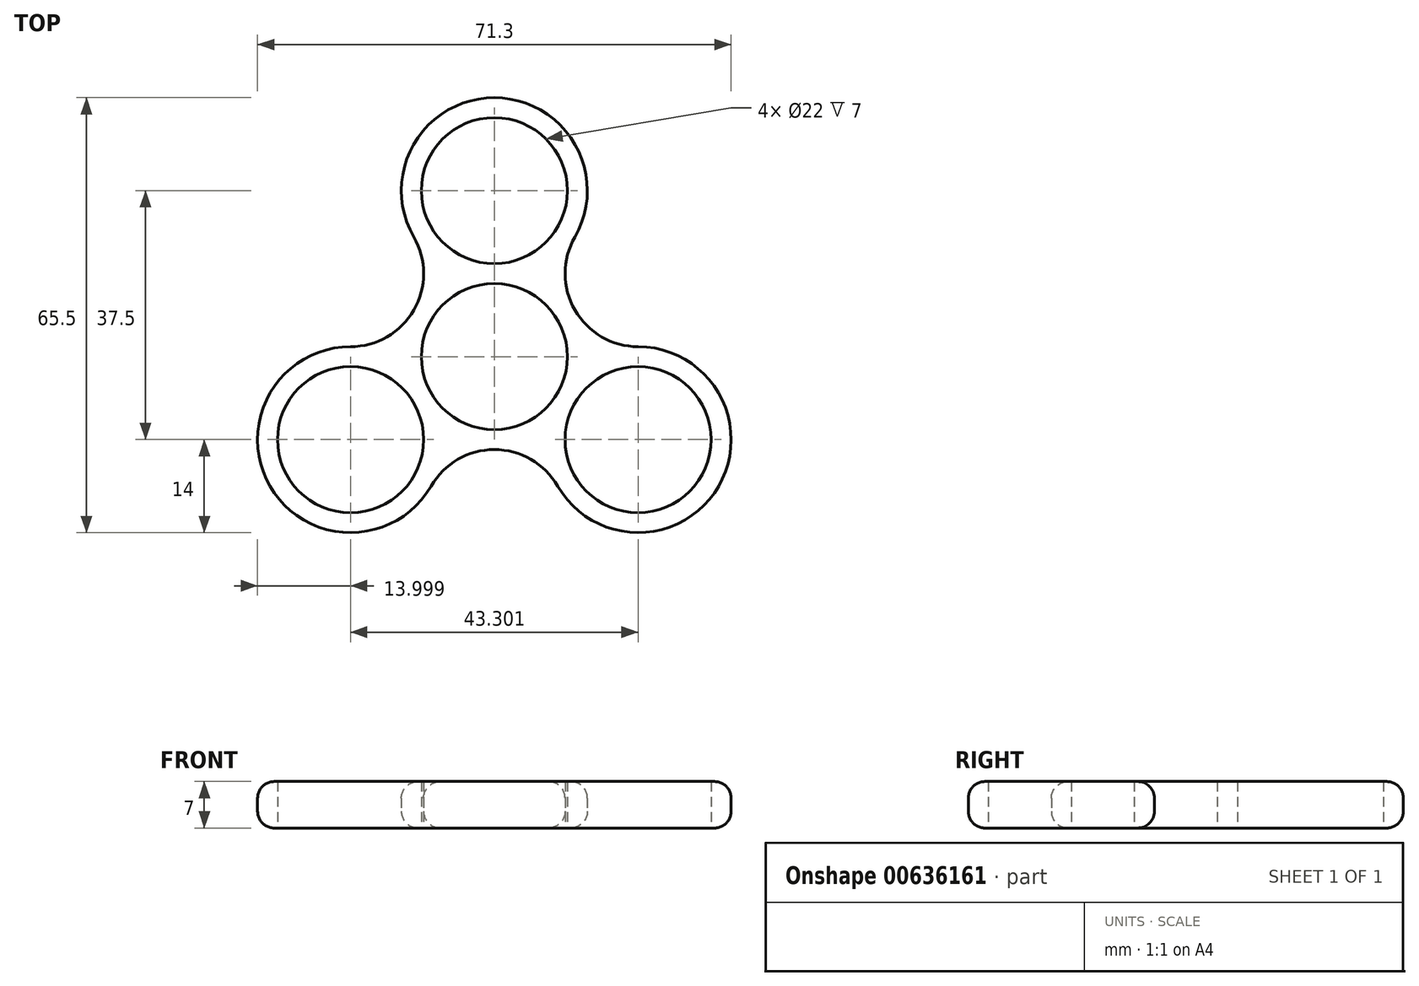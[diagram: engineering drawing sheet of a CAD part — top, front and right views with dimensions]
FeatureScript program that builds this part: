
annotation { "Feature Type Name" : "Feature", "Feature Type Description" : "" }
export const myFeature = defineFeature(function(context is Context, id is Id, definition is map)
    precondition{}
    {
        {
            var Q0;
            Q0=qCreatedBy(makeId("Top.planeOp"),FACE);
            var sketch = newSketch(context, id + "F0", { "sketchPlane" : qUnion([Q0])});
            skCircle(sketch, "E0", {"center": v(0, 0) * mm, "radius": 11 * mm});
            skCircle(sketch, "E1", {"center": v(0, 0) * mm, "radius": 25 * mm});
            skCircle(sketch, "E2", {"center": v(0, 0) * mm, "radius": 39 * mm});
            skCircle(sketch, "E3", {"center": v(0, 25) * mm, "radius": 11 * mm});
            skCircle(sketch, "E4.1.0", {"center": v(-21.65, 12.5) * mm, "radius": 11 * mm});
            skCircle(sketch, "E4.2.0", {"center": v(-21.65, -12.5) * mm, "radius": 11 * mm});
            skCircle(sketch, "E4.3.0", {"center": v(0, -25) * mm, "radius": 11 * mm});
            skCircle(sketch, "E4.4.0", {"center": v(21.65, -12.5) * mm, "radius": 11 * mm});
            skCircle(sketch, "E4.5.0", {"center": v(21.65, 12.5) * mm, "radius": 11 * mm});
            skCircle(sketch, "E5", {"center": v(0, 25) * mm, "radius": 14 * mm});
            skCircle(sketch, "E6.1.0", {"center": v(-21.65, -12.5) * mm, "radius": 14 * mm});
            skCircle(sketch, "E6.2.0", {"center": v(21.65, -12.5) * mm, "radius": 14 * mm});
            skSolve(sketch);
        }
        {
            var Q0;
            {var subQ0=sQuery(id+"F0.wireOp",EDGE,"E5");var subQ2=sQuery(id+"F0.wireOp",EDGE,"E1");var subQ7=makeQuery(id+"F0.imprint","INTERSECT",VERTEX,{"disambiguationData":[OD(0.0)],"derivedFrom":[subQ2,subQ0]});Q0=makeQuery(id+"F0.imprint","IMPRINT",FACE,{"disambiguationData":[TD([[makeQuery(id+"F0.imprint","IMPRINT",EDGE,{"disambiguationData":[TD([[subQ7,-1.0]])],"derivedFrom":subQ2}),-1.0]])]});}
            var Q1;
            {var subQ0=sQuery(id+"F0.wireOp",EDGE,"E6.1.0");var subQ2=sQuery(id+"F0.wireOp",EDGE,"E1");var subQ7=makeQuery(id+"F0.imprint","INTERSECT",VERTEX,{"disambiguationData":[OD(0.0)],"derivedFrom":[subQ2,subQ0]});Q1=makeQuery(id+"F0.imprint","IMPRINT",FACE,{"disambiguationData":[TD([[makeQuery(id+"F0.imprint","IMPRINT",EDGE,{"disambiguationData":[TD([[subQ7,-1.0]])],"derivedFrom":subQ2}),-1.0]])]});}
            var Q2;
            {var subQ0=sQuery(id+"F0.wireOp",EDGE,"E6.2.0");var subQ2=sQuery(id+"F0.wireOp",EDGE,"E1");var subQ7=makeQuery(id+"F0.imprint","INTERSECT",VERTEX,{"disambiguationData":[OD(1.0)],"derivedFrom":[subQ2,subQ0]});Q2=makeQuery(id+"F0.imprint","IMPRINT",FACE,{"disambiguationData":[TD([[makeQuery(id+"F0.imprint","IMPRINT",EDGE,{"disambiguationData":[TD([[subQ7,-1.0]])],"derivedFrom":subQ2}),-1.0]])]});}
            var Q3;
            {var subQ1=sQuery(id+"F0.wireOp",EDGE,"E1");var subQ4=sQuery(id+"F0.wireOp",EDGE,"E6.1.0");var subQ5=makeQuery(id+"F0.imprint","INTERSECT",VERTEX,{"disambiguationData":[OD(0.0)],"derivedFrom":[subQ1,subQ4]});Q3=makeQuery(id+"F0.imprint","IMPRINT",FACE,{"disambiguationData":[TD([[makeQuery(id+"F0.imprint","IMPRINT",EDGE,{"disambiguationData":[TD([[subQ5,-1.0]])],"derivedFrom":subQ1}),1.0]])]});}
            var Q4;
            {var subQ1=sQuery(id+"F0.wireOp",EDGE,"E1");var subQ4=sQuery(id+"F0.wireOp",EDGE,"E6.2.0");var subQ5=makeQuery(id+"F0.imprint","INTERSECT",VERTEX,{"disambiguationData":[OD(1.0)],"derivedFrom":[subQ1,subQ4]});Q4=makeQuery(id+"F0.imprint","IMPRINT",FACE,{"disambiguationData":[TD([[makeQuery(id+"F0.imprint","IMPRINT",EDGE,{"disambiguationData":[TD([[subQ5,-1.0]])],"derivedFrom":subQ1}),1.0]])]});}
            var Q5;
            {var subQ1=sQuery(id+"F0.wireOp",EDGE,"E1");var subQ4=sQuery(id+"F0.wireOp",EDGE,"E5");var subQ5=makeQuery(id+"F0.imprint","INTERSECT",VERTEX,{"disambiguationData":[OD(0.0)],"derivedFrom":[subQ1,subQ4]});Q5=makeQuery(id+"F0.imprint","IMPRINT",FACE,{"disambiguationData":[TD([[makeQuery(id+"F0.imprint","IMPRINT",EDGE,{"disambiguationData":[TD([[subQ5,-1.0]])],"derivedFrom":subQ1}),1.0]])]});}
            var Q6;
            {var subQ0=sQuery(id+"F0.wireOp",EDGE,"E5");var subQ1=sQuery(id+"F0.wireOp",EDGE,"E0");var subQ2=makeQuery(id+"F0.imprint","INTERSECT",VERTEX,{"derivedFrom":[subQ1,subQ0]});Q6=makeQuery(id+"F0.imprint","IMPRINT",FACE,{"disambiguationData":[TD([[makeQuery(id+"F0.imprint","IMPRINT",EDGE,{"disambiguationData":[TD([[subQ2,1.0]])],"derivedFrom":subQ1}),-1.0]])]});}
            var Q7;
            {var subQ0=sQuery(id+"F0.wireOp",EDGE,"E6.1.0");var subQ1=sQuery(id+"F0.wireOp",EDGE,"E0");var subQ2=makeQuery(id+"F0.imprint","INTERSECT",VERTEX,{"derivedFrom":[subQ1,subQ0]});Q7=makeQuery(id+"F0.imprint","IMPRINT",FACE,{"disambiguationData":[TD([[makeQuery(id+"F0.imprint","IMPRINT",EDGE,{"disambiguationData":[TD([[subQ2,1.0]])],"derivedFrom":subQ1}),-1.0]])]});}
            var Q8;
            {var subQ0=sQuery(id+"F0.wireOp",EDGE,"E6.1.0");var subQ1=sQuery(id+"F0.wireOp",EDGE,"E0");var subQ2=makeQuery(id+"F0.imprint","INTERSECT",VERTEX,{"derivedFrom":[subQ1,subQ0]});Q8=makeQuery(id+"F0.imprint","IMPRINT",FACE,{"disambiguationData":[TD([[makeQuery(id+"F0.imprint","IMPRINT",EDGE,{"disambiguationData":[TD([[subQ2,-1.0]])],"derivedFrom":subQ1}),-1.0]])]});}
            extrude(context, id + "F1", {"entities" : qUnion([Q0, Q1, Q2, Q3, Q4, Q5, Q6, Q7, Q8]), "depth" : 7 * mm, "offsetDistance" : 25 * mm});
        }
        {
            var Q0;
            Q0=makeQuery(id+"F1.opExtrude","CAP_EDGE",EDGE,{"disambiguationData":[OSD([sQuery(id+"F0.wireOp",EDGE,"E6.1.0")])],"isStart":false});
            var Q1;
            Q1=makeQuery(id+"F1.opExtrude","CAP_EDGE",EDGE,{"disambiguationData":[OSD([sQuery(id+"F0.wireOp",EDGE,"E4.3.0")])],"isStart":true});
            fillet(context, id + "F2", {"entities" : qUnion([Q0, Q1]), "radius" : 2.5 * mm, "tangentPropagation" : true, "allowEdgeOverflow" : false});
        }
    });
